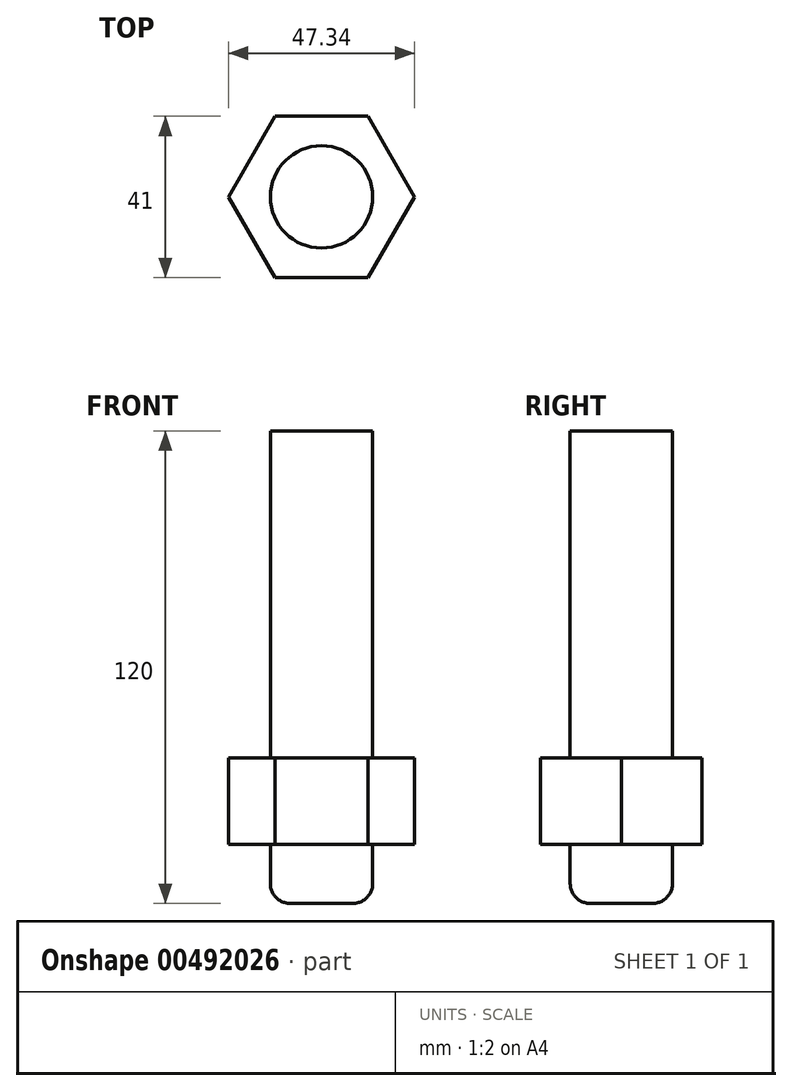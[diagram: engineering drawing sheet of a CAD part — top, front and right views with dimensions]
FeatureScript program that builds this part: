
annotation { "Feature Type Name" : "Feature", "Feature Type Description" : "" }
export const myFeature = defineFeature(function(context is Context, id is Id, definition is map)
    precondition{}
    {
        {
            var Q0;
            Q0=qCreatedBy(makeId("Top.planeOp"),FACE);
            var sketch = newSketch(context, id + "F0", { "sketchPlane" : qUnion([Q0])});
            skCircle(sketch, "E0", {"center": v(0, 0) * mm, "radius": 13 * mm});
            skSolve(sketch);
        }
        {
            var Q0;
            Q0=makeQuery(id+"F0.imprint","IMPRINT",FACE,{"disambiguationData":[TD([[makeQuery(id+"F0.imprint","IMPRINT",EDGE,{"derivedFrom":sQuery(id+"F0.wireOp",EDGE,"E0")}),1.0]])]});
            extrude(context, id + "F1", {"entities" : qUnion([Q0]), "depth" : 120 * mm});
        }
        {
            var Q0;
            Q0=makeQuery(id+"F1.opExtrude","CAP_EDGE",EDGE,{"disambiguationData":[OSD([sQuery(id+"F0.wireOp",EDGE,"E0")])],"isStart":true});
            fillet(context, id + "F2", {"entities" : qUnion([Q0]), "radius" : 5 * mm, "tangentPropagation" : true, "allowEdgeOverflow" : false});
        }
        {
            var Q0;
            Q0=qCreatedBy(makeId("Top.planeOp"),FACE);
            cPlane(context, id + "F3", {"entities" : qUnion([Q0]), "cplaneType" : CPlaneType.OFFSET, "offset" : 15 * mm, "width" : 150 * mm, "height" : 150 * mm});
        }
        {
            var Q0;
            Q0=qCreatedBy(id+"F3.planeOp",FACE);
            var sketch = newSketch(context, id + "F4", { "sketchPlane" : qUnion([Q0])});
            skCircle(sketch, "E1", {"center": v(0, 0) * mm, "radius": 13 * mm});
            skCircle(sketch, "E2.cCircle", {"center": v(0, 0) * mm, "radius": 20.5 * mm, "construction": true});
            skLineSegment(sketch, "E2.0", {"start": v(-11.84, 20.5) * mm, "end": v(11.84, 20.5) * mm});
            skLineSegment(sketch, "E2.1", {"start": v(11.84, 20.5) * mm, "end": v(23.67, 0) * mm});
            skLineSegment(sketch, "E2.2", {"start": v(23.67, 0) * mm, "end": v(11.84, -20.5) * mm});
            skLineSegment(sketch, "E2.3", {"start": v(11.84, -20.5) * mm, "end": v(-11.84, -20.5) * mm});
            skLineSegment(sketch, "E2.4", {"start": v(-11.84, -20.5) * mm, "end": v(-23.67, 0) * mm});
            skLineSegment(sketch, "E2.5", {"start": v(-23.67, 0) * mm, "end": v(-11.84, 20.5) * mm});
            skPoint(sketch, "E2.0.midPoint", {"position": v(0, 20.5) * mm});
            skSolve(sketch);
        }
        {
            var Q0;
            Q0 = qSketchRegion(id + "F4", true);
            extrude(context, id + "F5", {"entities" : qUnion([Q0]), "operationType" : NewBodyOperationType.ADD, "depth" : 22 * mm});
        }
    });
